# Revit family: FantiniCosmi_BIM_K10C6KIT
name_source: partatom
category: Generic Models
units: mm (PartAtom-declared; Revit-internal decimal feet)

## family parameters
Always vertical = Yes
Can host rebar = No
Cut with Voids When Loaded = No
Part Type = Normal
Room Calculation Point = No
Round Connector Dimension = Use Diameter
Shared = No
Work Plane-Based = No

## types (1)
- Standard
    Cable diameter = 9 mm
    Cable length = 6 m
    Catalog web link = https://www.fantinicosmi.it
    Compliant with Directive = 2014/35/EU
    Complying with Standard = EN60335-1
    Constant power delivered = ~10W/m
    Default Elevation = 0 mm  [stored 0 ft]
    Description = Antifreeze heating cable kit with constant antifreeze power
    Maximum room temperature powered = 65 °C
    Minimum installation room temperature = -5 °C
    Minimum storage room temperature = -20 ÷ -25°C
    Part Number = K10C6KIT
    Power supply = 230V-50Hz
    Protection rating = IPX7
    Thermostat temperature scale = ON +5°C / OFF +15°C

note: [stored X ft] marks values corroborated as IEEE doubles in the binary element streams (Revit-internal decimal feet)

## geometry (parser evidence)
native form markers: Sweep x3
no freeform markers — native parametric forms only
